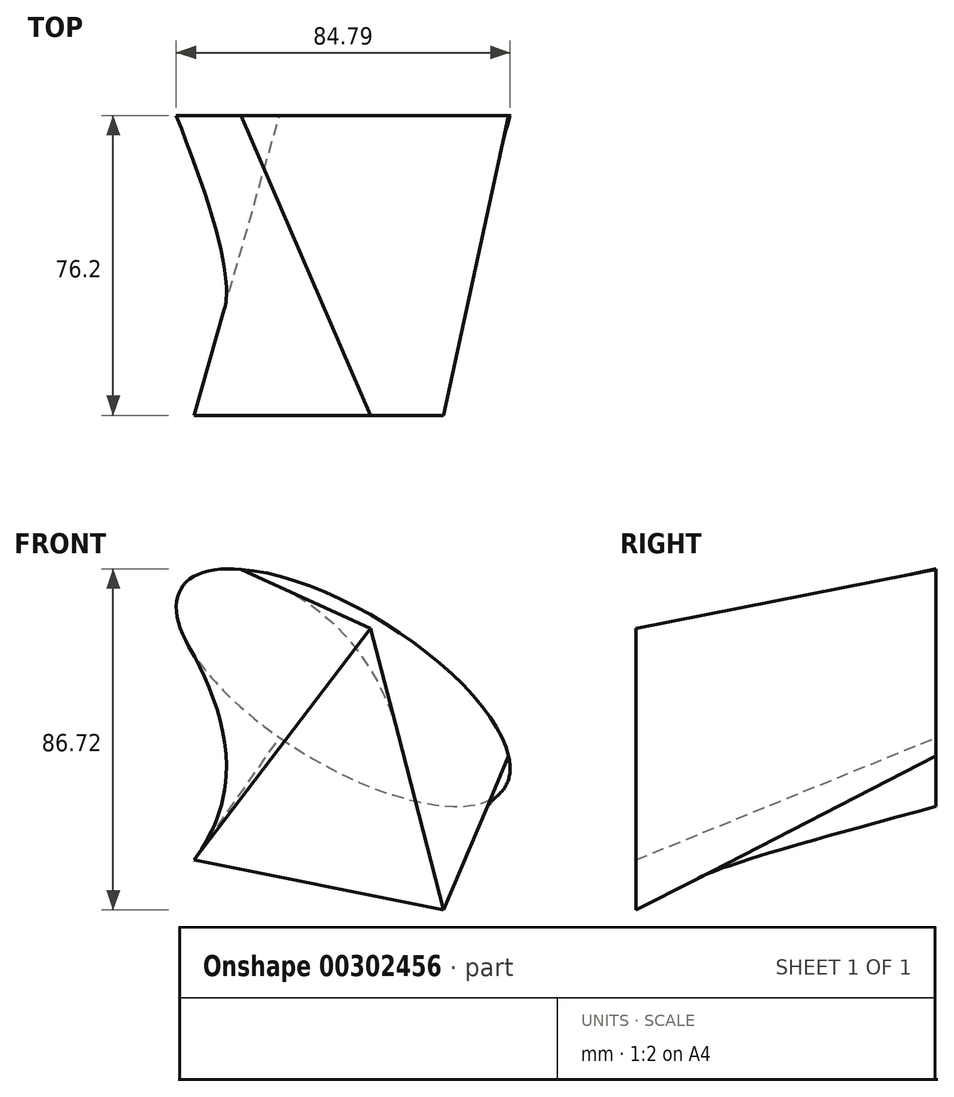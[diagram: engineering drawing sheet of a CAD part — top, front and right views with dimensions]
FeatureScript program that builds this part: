
annotation { "Feature Type Name" : "Feature", "Feature Type Description" : "" }
export const myFeature = defineFeature(function(context is Context, id is Id, definition is map)
    precondition{}
    {
        {
            var Q0;
            Q0=qCreatedBy(makeId("Front.planeOp"),FACE);
            var sketch = newSketch(context, id + "F0", { "sketchPlane" : qUnion([Q0])});
            skEllipse(sketch, "E0", {"center": v(-68.32, 43.78) * mm, "majorRadius": 48.26 * mm, "minorRadius": 19.49 * mm, "majorAxis": v(0.85, -0.52)});
            skSolve(sketch);
        }
        {
            var Q0;
            Q0=qCreatedBy(makeId("Front.planeOp"),FACE);
            cPlane(context, id + "F1", {"entities" : qUnion([Q0]), "cplaneType" : CPlaneType.OFFSET, "offset" : 76.2 * mm, "width" : 152.4 * mm, "height" : 152.4 * mm});
        }
        {
            var Q0;
            Q0=qCreatedBy(id+"F1.planeOp",FACE);
            var sketch = newSketch(context, id + "F2", { "sketchPlane" : qUnion([Q0])});
            skLineSegment(sketch, "E1", {"start": v(-106.17, 0) * mm, "end": v(-61.37, 58.82) * mm});
            skLineSegment(sketch, "E2", {"start": v(-61.37, 58.82) * mm, "end": v(-42.79, -12.75) * mm});
            skLineSegment(sketch, "E3", {"start": v(-42.79, -12.75) * mm, "end": v(-106.17, 0) * mm});
            skSolve(sketch);
        }
        {
            var Q0;
            Q0=makeQuery(id+"F2.imprint","IMPRINT",FACE,{"disambiguationData":[TD([[makeQuery(id+"F2.imprint","IMPRINT",EDGE,{"derivedFrom":sQuery(id+"F2.wireOp",EDGE,"E1")}),-1.0]])]});
            var Q1;
            Q1=makeQuery(id+"F0.imprint","IMPRINT",FACE,{"disambiguationData":[TD([[makeQuery(id+"F0.imprint","IMPRINT",EDGE,{"derivedFrom":sQuery(id+"F0.wireOp",EDGE,"E0")}),1.0]])]});
            loft(context, id + "F3", {"sheetProfilesArray" : [{ "sheetProfileEntities" : qUnion([Q0]) }, { "sheetProfileEntities" : qUnion([Q1]) }]});
        }
    });
